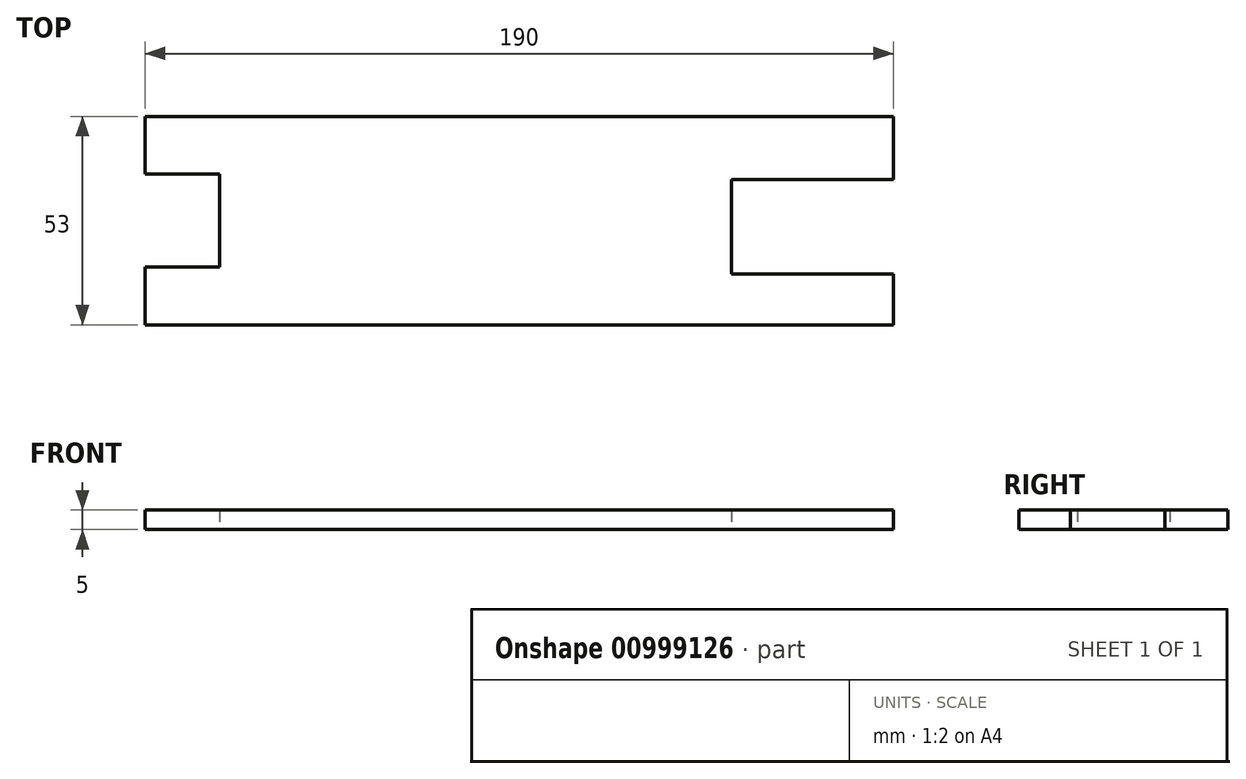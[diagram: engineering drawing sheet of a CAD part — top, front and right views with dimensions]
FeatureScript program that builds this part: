
annotation { "Feature Type Name" : "Feature", "Feature Type Description" : "" }
export const myFeature = defineFeature(function(context is Context, id is Id, definition is map)
    precondition{}
    {
        {
            var Q0;
            Q0=qCreatedBy(makeId("Top.planeOp"),FACE);
            var sketch = newSketch(context, id + "F0", { "sketchPlane" : qUnion([Q0])});
            skLineSegment(sketch, "E0.bottom", {"start": v(-93.87, 26.43) * mm, "end": v(96.13, 26.43) * mm});
            skLineSegment(sketch, "E0.top", {"start": v(-93.87, -26.57) * mm, "end": v(96.13, -26.57) * mm});
            skLineSegment(sketch, "E0.left", {"start": v(-93.87, 26.43) * mm, "end": v(-93.87, -26.57) * mm});
            skLineSegment(sketch, "E0.right", {"start": v(96.13, 26.43) * mm, "end": v(96.13, -26.57) * mm});
            skLineSegment(sketch, "E1.left", {"start": v(-93.87, -0.07) * mm, "end": v(-93.87, -14.37) * mm});
            skLineSegment(sketch, "E2.bottom", {"start": v(-67.43, 51.16) * mm, "end": v(-67.43, 51.16) * mm});
            skLineSegment(sketch, "E2.top", {"start": v(-67.43, -14.37) * mm, "end": v(-67.43, -14.37) * mm});
            skPoint(sketch, "E1.right.start.orphan", {"position": v(-67.43, -0.07) * mm});
            skLineSegment(sketch, "E3.bottom", {"start": v(-93.87, 11.7) * mm, "end": v(-74.97, 11.7) * mm});
            skLineSegment(sketch, "E3.top", {"start": v(-93.87, -11.83) * mm, "end": v(-74.97, -11.83) * mm});
            skLineSegment(sketch, "E3.left", {"start": v(-93.87, 11.7) * mm, "end": v(-93.87, -11.83) * mm});
            skLineSegment(sketch, "E3.right", {"start": v(-74.97, 11.7) * mm, "end": v(-74.97, -11.83) * mm});
            skLineSegment(sketch, "E4.bottom", {"start": v(96.13, 10.38) * mm, "end": v(55.02, 10.38) * mm});
            skLineSegment(sketch, "E4.top", {"start": v(96.13, -13.6) * mm, "end": v(55.02, -13.6) * mm});
            skLineSegment(sketch, "E4.left", {"start": v(96.13, 10.38) * mm, "end": v(96.13, -13.6) * mm});
            skLineSegment(sketch, "E4.right", {"start": v(55.02, 10.38) * mm, "end": v(55.02, -13.6) * mm});
            skSolve(sketch);
        }
        {
            var Q0;
            Q0=makeQuery(id+"F0.imprint","IMPRINT",FACE,{"disambiguationData":[TD([[makeQuery(id+"F0.imprint","IMPRINT",EDGE,{"derivedFrom":sQuery(id+"F0.wireOp",EDGE,"E0.bottom")}),-1.0]])]});
            extrude(context, id + "F1", {"entities" : qUnion([Q0]), "depth" : 5 * mm, "offsetDistance" : 25 * mm});
        }
        {
            var Q0;
            Q0 = qSketchRegion(id + "F0", true);
            extrude(context, id + "F2", {"entities" : qUnion([Q0]), "operationType" : NewBodyOperationType.REMOVE, "oppositeDirection" : true, "depth" : 25 * mm, "offsetDistance" : 25 * mm});
        }
        {
            var Q0;
            Q0 = qSketchRegion(id + "F0", true);
            extrude(context, id + "F3", {"entities" : qUnion([Q0]), "operationType" : NewBodyOperationType.REMOVE, "oppositeDirection" : true, "depth" : 25 * mm, "offsetDistance" : 25 * mm});
        }
    });
